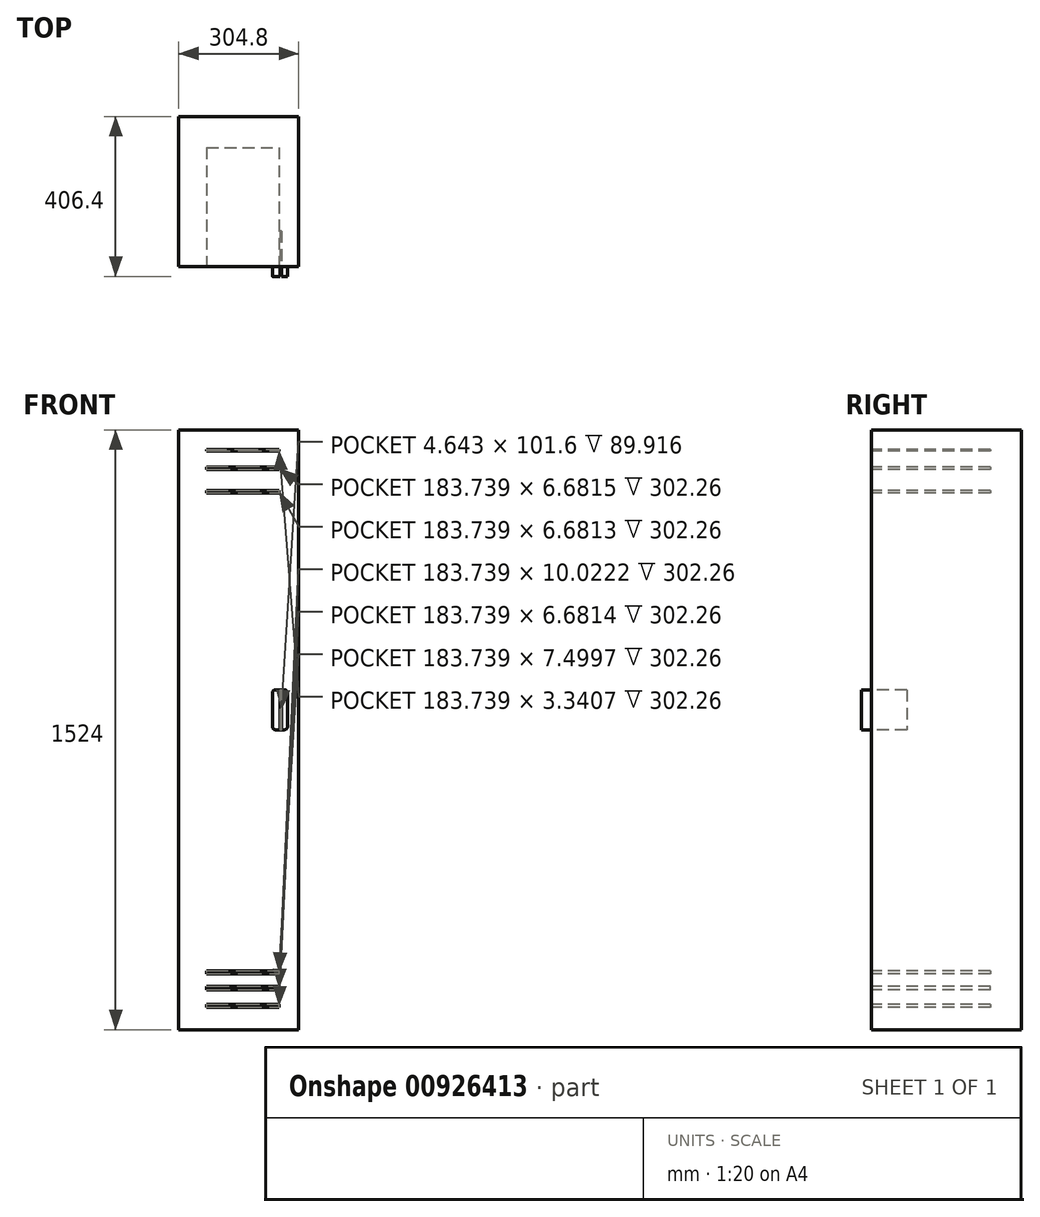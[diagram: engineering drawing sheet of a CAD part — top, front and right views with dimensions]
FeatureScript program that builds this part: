
annotation { "Feature Type Name" : "Feature", "Feature Type Description" : "" }
export const myFeature = defineFeature(function(context is Context, id is Id, definition is map)
    precondition{}
    {
        {
            var Q0;
            Q0=qCreatedBy(makeId("Front.planeOp"),FACE);
            var sketch = newSketch(context, id + "F0", { "sketchPlane" : qUnion([Q0])});
            skLineSegment(sketch, "E0.bottom", {"start": v(-144.88, 1260.45) * mm, "end": v(159.92, 1260.45) * mm});
            skLineSegment(sketch, "E0.top", {"start": v(-144.88, -263.55) * mm, "end": v(159.92, -263.55) * mm});
            skLineSegment(sketch, "E0.left", {"start": v(-144.88, 1260.45) * mm, "end": v(-144.88, -263.55) * mm});
            skLineSegment(sketch, "E0.right", {"start": v(159.92, 1260.45) * mm, "end": v(159.92, -263.55) * mm});
            skSolve(sketch);
        }
        {
            var Q0;
            Q0 = qSketchRegion(id + "F0", true);
            extrude(context, id + "F1", {"entities" : qUnion([Q0]), "depth" : 381 * mm, "offsetDistance" : 25.4 * mm});
        }
        {
            var Q0;
            Q0=makeQuery(id+"F1.opExtrude","CAP_FACE",FACE,{"disambiguationData":[OSD([sQuery(id+"F0.wireOp",EDGE,"E0.bottom"),sQuery(id+"F0.wireOp",EDGE,"E0.top"),sQuery(id+"F0.wireOp",EDGE,"E0.left"),sQuery(id+"F0.wireOp",EDGE,"E0.right")])],"isStart":false});
            var sketch = newSketch(context, id + "F2", { "sketchPlane" : qUnion([Q0])});
            skLineSegment(sketch, "E1", {"start": v(0, 1260.45) * mm, "end": v(0, 498.45) * mm, "construction": true});
            skLineSegment(sketch, "E2.bottom", {"start": v(123.55, 498.45) * mm, "end": v(100.7, 498.45) * mm});
            skLineSegment(sketch, "E2.top", {"start": v(123.55, 600.05) * mm, "end": v(100.7, 600.05) * mm});
            skLineSegment(sketch, "E2.left", {"start": v(131.17, 506.07) * mm, "end": v(131.17, 592.43) * mm});
            skLineSegment(sketch, "E2.right", {"start": v(93.07, 506.07) * mm, "end": v(93.07, 592.43) * mm});
            skPoint(sketch, "E3.visualSharp", {"position": v(131.17, 600.05) * mm});
            skArc(sketch, "E3.filletArc", {"start": v(131.17, 592.43) * mm, "mid": v(128.94, 597.81) * mm, "end": v(123.55, 600.05) * mm});
            skPoint(sketch, "E4.visualSharp", {"position": v(93.07, 600.05) * mm});
            skArc(sketch, "E4.filletArc", {"start": v(100.7, 600.05) * mm, "mid": v(95.3, 597.81) * mm, "end": v(93.07, 592.43) * mm});
            skPoint(sketch, "E5.visualSharp", {"position": v(131.17, 498.45) * mm});
            skArc(sketch, "E5.filletArc", {"start": v(123.55, 498.45) * mm, "mid": v(128.94, 500.68) * mm, "end": v(131.17, 506.07) * mm});
            skPoint(sketch, "E6.visualSharp", {"position": v(93.07, 498.45) * mm});
            skArc(sketch, "E6.filletArc", {"start": v(93.07, 506.07) * mm, "mid": v(95.3, 500.68) * mm, "end": v(100.7, 498.45) * mm});
            skSolve(sketch);
        }
        {
            var Q0;
            Q0 = qSketchRegion(id + "F2", true);
            extrude(context, id + "F3", {"entities" : qUnion([Q0]), "operationType" : NewBodyOperationType.ADD, "depth" : 25.4 * mm, "offsetDistance" : 25.4 * mm});
        }
        {
            var Q0;
            Q0=makeQuery(id+"F3.opExtrude","CAP_FACE",FACE,{"disambiguationData":[OSD([sQuery(id+"F2.wireOp",EDGE,"E2.bottom"),sQuery(id+"F2.wireOp",EDGE,"E2.top"),sQuery(id+"F2.wireOp",EDGE,"E2.left"),sQuery(id+"F2.wireOp",EDGE,"E2.right")])],"isStart":false});
            var sketch = newSketch(context, id + "F4", { "sketchPlane" : qUnion([Q0])});
            skLineSegment(sketch, "E7.bottom", {"start": v(112.12, 600.05) * mm, "end": v(116.76, 600.05) * mm});
            skLineSegment(sketch, "E7.top", {"start": v(112.12, 498.45) * mm, "end": v(116.76, 498.45) * mm});
            skLineSegment(sketch, "E7.left", {"start": v(112.12, 600.05) * mm, "end": v(112.12, 498.45) * mm});
            skLineSegment(sketch, "E7.right", {"start": v(116.76, 600.05) * mm, "end": v(116.76, 498.45) * mm});
            skPoint(sketch, "E8.centerSnap0", {"position": v(116.76, 549.25) * mm});
            skSolve(sketch);
        }
        {
            var Q0;
            Q0=makeQuery(id+"F4.imprint","IMPRINT",FACE,{"disambiguationData":[TD([[makeQuery(id+"F4.imprint","IMPRINT",EDGE,{"derivedFrom":sQuery(id+"F4.wireOp",EDGE,"E7.bottom")}),1.0]])]});
            extrude(context, id + "F5", {"entities" : qUnion([Q0]), "operationType" : NewBodyOperationType.REMOVE, "oppositeDirection" : true, "depth" : 115.32 * mm, "offsetDistance" : 25.4 * mm});
        }
        {
            var Q0;
            Q0=makeQuery(id+"F1.opExtrude","CAP_FACE",FACE,{"disambiguationData":[OSD([sQuery(id+"F0.wireOp",EDGE,"E0.bottom"),sQuery(id+"F0.wireOp",EDGE,"E0.top"),sQuery(id+"F0.wireOp",EDGE,"E0.left"),sQuery(id+"F0.wireOp",EDGE,"E0.right")])],"isStart":false});
            var sketch = newSketch(context, id + "F6", { "sketchPlane" : qUnion([Q0])});
            skLineSegment(sketch, "E9.bottom", {"start": v(-74.33, 1210.02) * mm, "end": v(109.41, 1210.02) * mm});
            skLineSegment(sketch, "E9.top", {"start": v(-74.33, 1206.68) * mm, "end": v(109.41, 1206.68) * mm});
            skLineSegment(sketch, "E9.left", {"start": v(-74.33, 1210.02) * mm, "end": v(-74.33, 1206.68) * mm});
            skLineSegment(sketch, "E9.right", {"start": v(109.41, 1210.02) * mm, "end": v(109.41, 1206.68) * mm});
            skLineSegment(sketch, "E10.bottom", {"start": v(-74.33, 1166.59) * mm, "end": v(109.41, 1166.59) * mm});
            skLineSegment(sketch, "E10.top", {"start": v(-74.33, 1159.9) * mm, "end": v(109.41, 1159.9) * mm});
            skLineSegment(sketch, "E10.left", {"start": v(-74.33, 1166.59) * mm, "end": v(-74.33, 1159.9) * mm});
            skLineSegment(sketch, "E10.right", {"start": v(109.41, 1166.59) * mm, "end": v(109.41, 1159.9) * mm});
            skLineSegment(sketch, "E11.bottom", {"start": v(-74.33, 1106.45) * mm, "end": v(109.41, 1106.45) * mm});
            skLineSegment(sketch, "E11.top", {"start": v(-74.33, 1099.77) * mm, "end": v(109.41, 1099.77) * mm});
            skLineSegment(sketch, "E11.left", {"start": v(-74.33, 1106.45) * mm, "end": v(-74.33, 1099.77) * mm});
            skLineSegment(sketch, "E11.right", {"start": v(109.41, 1106.45) * mm, "end": v(109.41, 1099.77) * mm});
            skLineSegment(sketch, "E12.bottom", {"start": v(-74.33, -163.01) * mm, "end": v(109.41, -163.01) * mm});
            skLineSegment(sketch, "E12.top", {"start": v(-74.33, -153) * mm, "end": v(109.41, -153) * mm});
            skLineSegment(sketch, "E12.left", {"start": v(-74.33, -163.01) * mm, "end": v(-74.33, -153) * mm});
            skLineSegment(sketch, "E12.right", {"start": v(109.41, -163.01) * mm, "end": v(109.41, -153) * mm});
            skLineSegment(sketch, "E13.bottom", {"start": v(-74.33, -199.76) * mm, "end": v(109.41, -199.76) * mm});
            skLineSegment(sketch, "E13.top", {"start": v(-74.33, -206.44) * mm, "end": v(109.41, -206.44) * mm});
            skLineSegment(sketch, "E13.left", {"start": v(-74.33, -199.76) * mm, "end": v(-74.33, -206.44) * mm});
            skLineSegment(sketch, "E13.right", {"start": v(109.41, -199.76) * mm, "end": v(109.41, -206.44) * mm});
            skLineSegment(sketch, "E14.bottom", {"start": v(-74.33, -113.7) * mm, "end": v(109.41, -113.7) * mm});
            skLineSegment(sketch, "E14.top", {"start": v(-74.33, -121.2) * mm, "end": v(109.41, -121.2) * mm});
            skLineSegment(sketch, "E14.left", {"start": v(-74.33, -113.7) * mm, "end": v(-74.33, -121.2) * mm});
            skLineSegment(sketch, "E14.right", {"start": v(109.41, -113.7) * mm, "end": v(109.41, -121.2) * mm});
            skSolve(sketch);
        }
        {
            var Q0;
            Q0 = qSketchRegion(id + "F6", true);
            extrude(context, id + "F7", {"entities" : qUnion([Q0]), "operationType" : NewBodyOperationType.REMOVE, "oppositeDirection" : true, "depth" : 302.26 * mm, "offsetDistance" : 25.4 * mm});
        }
    });
